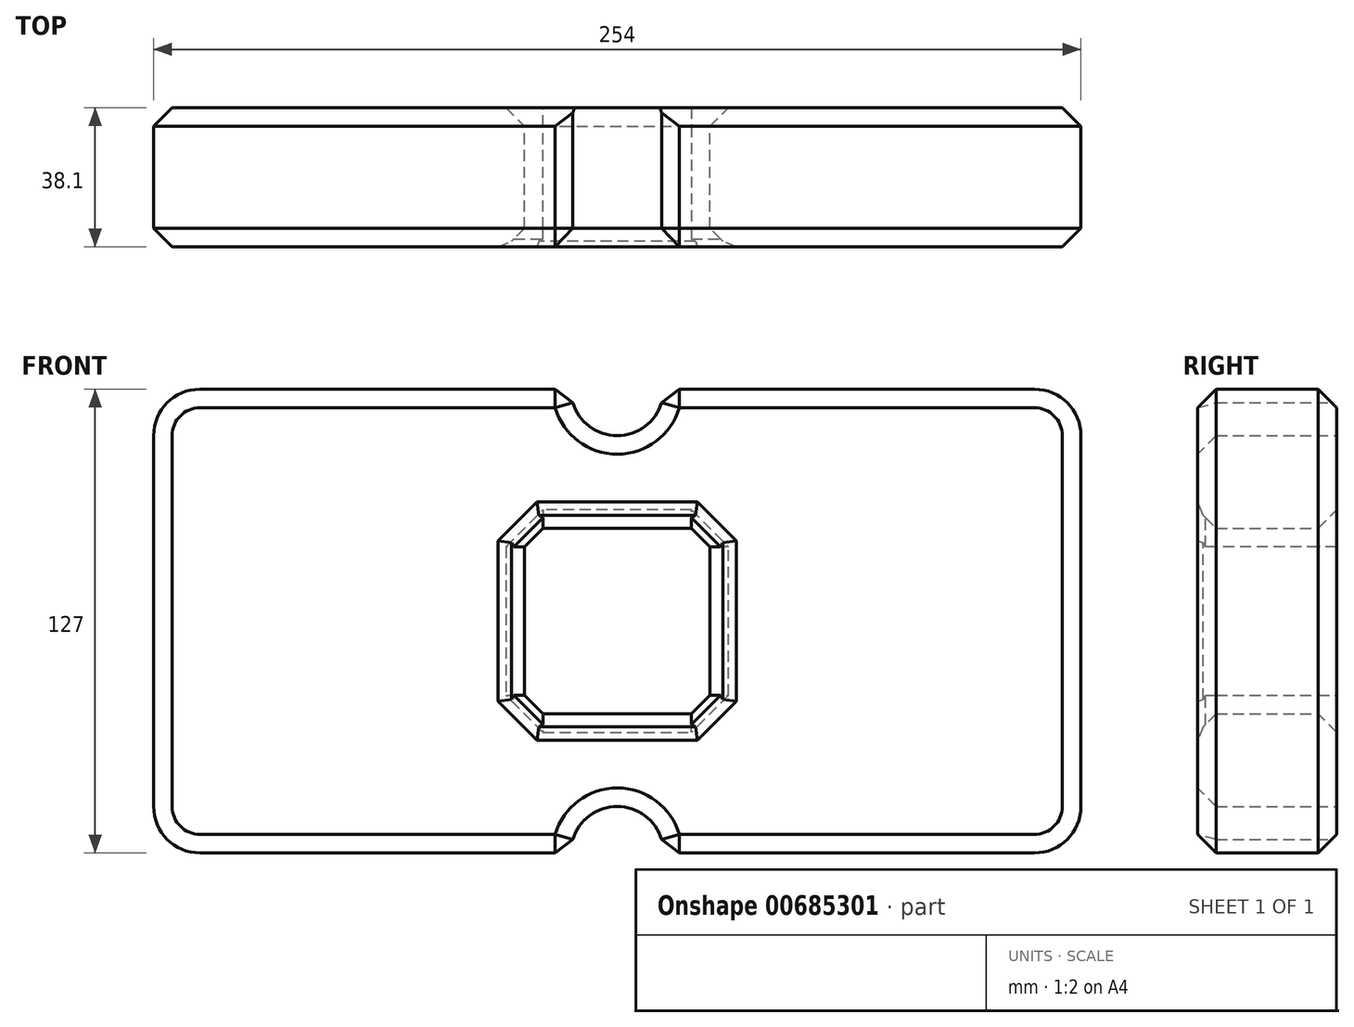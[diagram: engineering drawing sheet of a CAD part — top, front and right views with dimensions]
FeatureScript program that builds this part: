
annotation { "Feature Type Name" : "Feature", "Feature Type Description" : "" }
export const myFeature = defineFeature(function(context is Context, id is Id, definition is map)
    precondition{}
    {
        {
            var Q0;
            Q0=qCreatedBy(makeId("Front.planeOp"),FACE);
            var sketch = newSketch(context, id + "F0", { "sketchPlane" : qUnion([Q0])});
            skLineSegment(sketch, "E0.top", {"start": v(-111.05, -60.86) * mm, "end": v(-9.45, -60.86) * mm});
            skLineSegment(sketch, "E0.left", {"start": v(-123.75, 53.44) * mm, "end": v(-123.75, -48.16) * mm});
            skLineSegment(sketch, "E0.right", {"start": v(130.25, 53.44) * mm, "end": v(130.25, -48.16) * mm});
            skLineSegment(sketch, "E1", {"start": v(-111.05, 66.14) * mm, "end": v(-9.45, 66.14) * mm});
            skPoint(sketch, "E2.visualSharp", {"position": v(-123.75, 66.14) * mm});
            skArc(sketch, "E2.filletArc", {"start": v(-111.05, 66.14) * mm, "mid": v(-120.03, 62.43) * mm, "end": v(-123.75, 53.44) * mm});
            skPoint(sketch, "E3.visualSharp", {"position": v(130.25, 66.14) * mm});
            skArc(sketch, "E3.filletArc", {"start": v(130.25, 53.44) * mm, "mid": v(126.53, 62.43) * mm, "end": v(117.55, 66.14) * mm});
            skPoint(sketch, "E4.visualSharp", {"position": v(130.25, -60.86) * mm});
            skArc(sketch, "E4.filletArc", {"start": v(117.55, -60.86) * mm, "mid": v(126.53, -57.14) * mm, "end": v(130.25, -48.16) * mm});
            skPoint(sketch, "E5.visualSharp", {"position": v(-123.75, -60.86) * mm});
            skArc(sketch, "E5.filletArc", {"start": v(-123.75, -48.16) * mm, "mid": v(-120.03, -57.14) * mm, "end": v(-111.05, -60.86) * mm});
            skArc(sketch, "E6", {"start": v(-9.45, 66.14) * mm, "mid": v(3.25, 53.44) * mm, "end": v(15.95, 66.14) * mm});
            skLineSegment(sketch, "E7.trimOffspring", {"start": v(15.95, 66.14) * mm, "end": v(117.55, 66.14) * mm});
            skArc(sketch, "E8", {"start": v(15.95, -60.86) * mm, "mid": v(3.25, -48.16) * mm, "end": v(-9.45, -60.86) * mm});
            skLineSegment(sketch, "E9.trimOffspring", {"start": v(15.95, -60.86) * mm, "end": v(117.55, -60.86) * mm});
            skLineSegment(sketch, "E10.bottom", {"start": v(-22.15, 28.04) * mm, "end": v(28.65, 28.04) * mm});
            skLineSegment(sketch, "E10.top", {"start": v(-22.15, -22.76) * mm, "end": v(28.65, -22.76) * mm});
            skLineSegment(sketch, "E10.left", {"start": v(-22.15, 28.04) * mm, "end": v(-22.15, -22.76) * mm});
            skLineSegment(sketch, "E10.right", {"start": v(28.65, 28.04) * mm, "end": v(28.65, -22.76) * mm});
            skSolve(sketch);
        }
        {
            var Q0;
            Q0 = qSketchRegion(id + "F0", true);
            extrude(context, id + "F1", {"entities" : qUnion([Q0]), "depth" : 38.1 * mm, "offsetDistance" : 25.4 * mm});
        }
        {
            var Q0;
            Q0=makeQuery(id+"F1.opExtrude","SWEPT_EDGE",EDGE,{"disambiguationData":[OSD([sQuery(id+"F0.wireOp",EDGE,"E10.bottom"),sQuery(id+"F0.wireOp",EDGE,"E10.right")])]});
            var Q1;
            Q1=makeQuery(id+"F1.opExtrude","SWEPT_FACE",FACE,{"disambiguationData":[OSD([sQuery(id+"F0.wireOp",EDGE,"E10.right")])]});
            var Q2;
            Q2=makeQuery(id+"F1.opExtrude","SWEPT_FACE",FACE,{"disambiguationData":[OSD([sQuery(id+"F0.wireOp",EDGE,"E10.top")])]});
            var Q3;
            Q3=makeQuery(id+"F1.opExtrude","SWEPT_FACE",FACE,{"disambiguationData":[OSD([sQuery(id+"F0.wireOp",EDGE,"E10.left")])]});
            var Q4;
            Q4=makeQuery(id+"F1.opExtrude","SWEPT_FACE",FACE,{"disambiguationData":[OSD([sQuery(id+"F0.wireOp",EDGE,"E10.bottom")])]});
            chamfer(context, id + "F2", {"entities" : qUnion([Q0, Q1, Q2, Q3, Q4]), "width" : 5.08 * mm, "tangentPropagation" : true});
        }
        {
            var Q0;
            Q0=makeQuery(id+"F1.opExtrude","SWEPT_FACE",FACE,{"disambiguationData":[OSD([sQuery(id+"F0.wireOp",EDGE,"E1")])]});
            var Q1;
            Q1=makeQuery(id+"F1.opExtrude","SWEPT_FACE",FACE,{"disambiguationData":[OSD([sQuery(id+"F0.wireOp",EDGE,"E7.trimOffspring")])]});
            var Q2;
            Q2=makeQuery(id+"F1.opExtrude","SWEPT_FACE",FACE,{"disambiguationData":[OSD([sQuery(id+"F0.wireOp",EDGE,"E0.right")])]});
            var Q3;
            Q3=makeQuery(id+"F1.opExtrude","SWEPT_FACE",FACE,{"disambiguationData":[OSD([sQuery(id+"F0.wireOp",EDGE,"E9.trimOffspring")])]});
            var Q4;
            Q4=makeQuery(id+"F1.opExtrude","SWEPT_FACE",FACE,{"disambiguationData":[OSD([sQuery(id+"F0.wireOp",EDGE,"E0.top")])]});
            var Q5;
            Q5=makeQuery(id+"F1.opExtrude","CAP_FACE",FACE,{"disambiguationData":[OSD([sQuery(id+"F0.wireOp",EDGE,"E0.top"),sQuery(id+"F0.wireOp",EDGE,"E0.left"),sQuery(id+"F0.wireOp",EDGE,"E0.right"),sQuery(id+"F0.wireOp",EDGE,"E1"),sQuery(id+"F0.wireOp",EDGE,"E2.filletArc"),sQuery(id+"F0.wireOp",EDGE,"E3.filletArc"),sQuery(id+"F0.wireOp",EDGE,"E4.filletArc"),sQuery(id+"F0.wireOp",EDGE,"E5.filletArc"),sQuery(id+"F0.wireOp",EDGE,"E6"),sQuery(id+"F0.wireOp",EDGE,"E7.trimOffspring"),sQuery(id+"F0.wireOp",EDGE,"E8"),sQuery(id+"F0.wireOp",EDGE,"E9.trimOffspring"),sQuery(id+"F0.wireOp",EDGE,"E10.bottom"),sQuery(id+"F0.wireOp",EDGE,"E10.top"),sQuery(id+"F0.wireOp",EDGE,"E10.left"),sQuery(id+"F0.wireOp",EDGE,"E10.right")])],"isStart":false});
            chamfer(context, id + "F3", {"entities" : qUnion([Q0, Q1, Q2, Q3, Q4, Q5]), "width" : 5.08 * mm, "tangentPropagation" : true});
        }
    });
